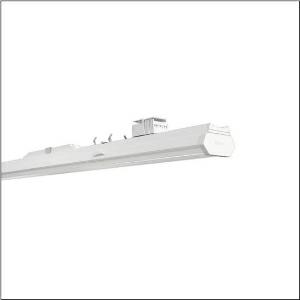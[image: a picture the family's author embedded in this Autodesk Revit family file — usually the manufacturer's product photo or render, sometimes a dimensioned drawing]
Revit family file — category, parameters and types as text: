
# Revit family: licross_r__11_protected_mo_51td12dn495g3c_9d50
name_source: partatom
category: Lighting Fixtures
units: mm (PartAtom-declared; Revit-internal decimal feet)

## family parameters
Cut with Voids When Loaded = No
Host = Face
Light Source = No
Part Type = Normal
Room Calculation Point = No
Round Connector Dimension = Use Diameter
Shared = No

## types (1)
- --- (1 x LED, 980 lm, 6.8 W, 4000K)
    Apparent Load = 7 VA
    CIE Flux Codes = 73 92 98 99 100
    Color Rendering = 80
    Color Temperature = 4000K
    Default Elevation = 1800 mm
    Description = Licross® 11 Protected MO, luminaire insert, of sheet steel, galvanised, coil coated, white, length: 1.500mm, width: 90mm, height: 101mm, LED rated luminous flux: 9.980lm, light colour: 840, control gear: DALI 2 (for two DALI lines), with plug, 6-pole, with phase selection, for trunking rail, 14-core, mains connection: 220..240V, AC, 50/60Hz, rated input power: 61W, for trunking rail, 14-core, internal wiring halogen-free, for emergency light function, converter,control gear: single battery element, battery: LiFePO4, 9Ah, primary light control with lens, of plastic, primary optical cover: cover, of PMMA, light emission: direct distribution, primary light characteristic: symmetric, protection rating (complete): IP54, insulation class (complete): insulation class I (protective earthing), certification: CE, UKCA, protection symbol: D if used in an environment with non-conductive dust loads with corresponding accessories, impact resistance: IK06, permissible ambient temperature for indoor applications: +5..+35°C, standard: EN 60598-2-22, LABS conformity tested according to VDMA 24364:2018-05, reducing of maximum allowable ambient temperature of 5°C with ceiling mounting, corresponds to IFS (International Featured Standards) requirements for safety and quality in the food industry, packaging unit: 1 piece
    Height = 92 mm
    Lamp = 1 x LED
    Lamp Light Flux = 980 lm
    Lamp Power = 6.8 W
    Lamp count = 1
    Length = 1500 mm
    Luminous efficacy = 144 lm/W
    Manufacturer = Siteco
    ModVariant = No
    Model = 51TD12DN495G3C
    Mounting Place = Ceiling
    Mounting Type = Pendant
    Number of Poles = 1
    OnlyDefault = Yes
    Power Factor = 1
    Product Name = Licross® 11 Protected MO
    Product group = luminaire insert | ceiling pendant
    ProductGroupID = 902
    Protection Class = Protection class I
    Protection Degree = IP 54
    RLX_Detail_Level = 1
    RLX_Emergency_Light_Flux = 0 lm
    RLX_Emergency_Type = 0
    RLX_Emergency_Type_DB = No
    RlxData = <blob elided: 24781 chars, md5=d2c248b2>
    Socket = socket
    Standby Power = 0 W
    System Light Flux = 980 lm
    System Power = 7 W
    Type Comments = : emergency light operation: 3 h
    Type Image = l_1256145.jpg
    URL = http://relux.com
    VarID = @adj_112191
    Voltage = 0 V
    Weight = 0.00 kg
    Width = 88 mm

## geometry (parser evidence)
native form markers: Blend x4, Sweep x11
no freeform markers — native parametric forms only
